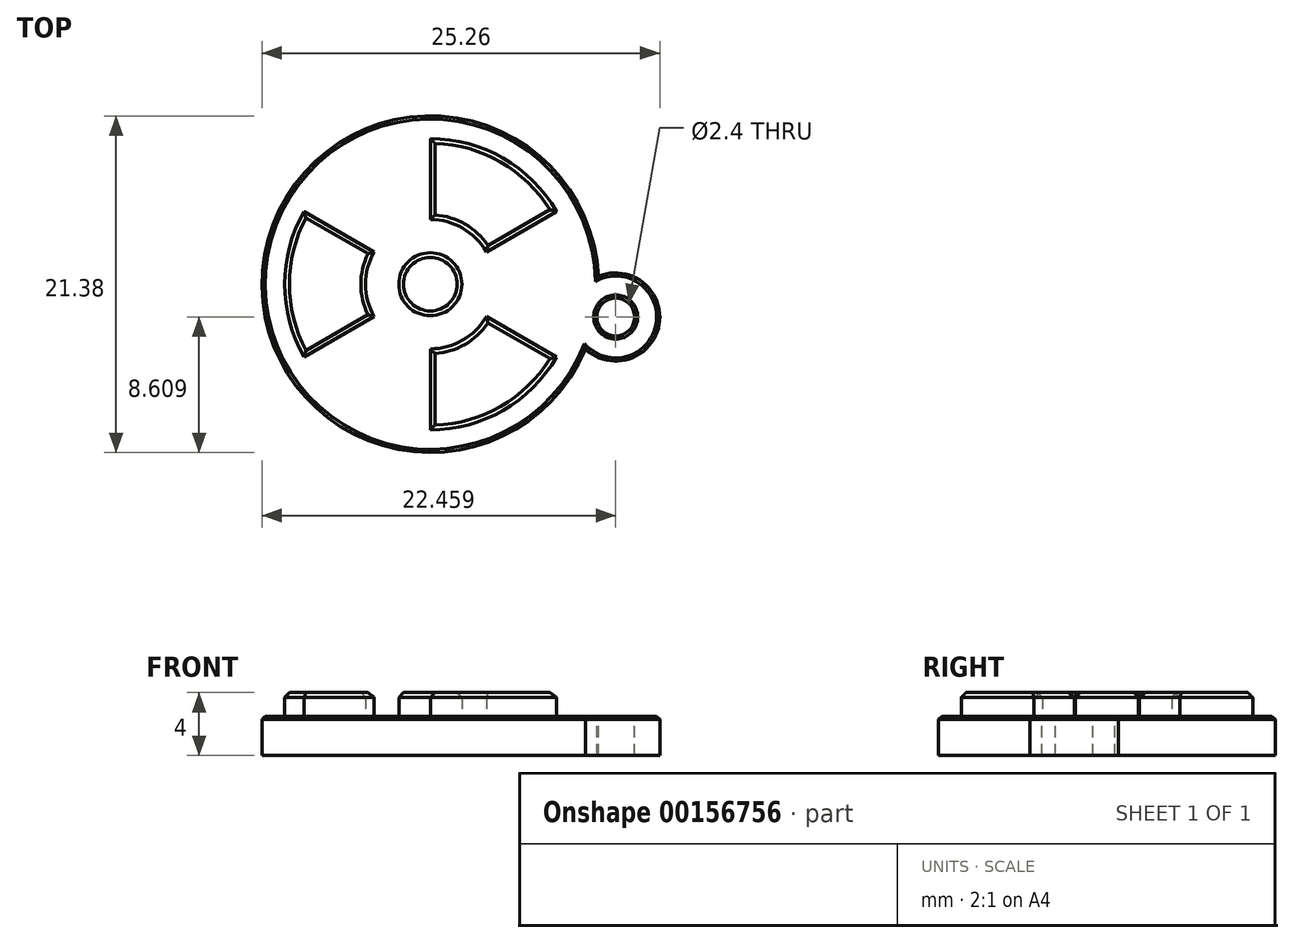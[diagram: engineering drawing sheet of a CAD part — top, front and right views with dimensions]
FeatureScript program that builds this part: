
annotation { "Feature Type Name" : "Feature", "Feature Type Description" : "" }
export const myFeature = defineFeature(function(context is Context, id is Id, definition is map)
    precondition{}
    {
        {
            var Q0;
            Q0=qCreatedBy(makeId("Top.planeOp"),FACE);
            var sketch = newSketch(context, id + "F0", { "sketchPlane" : qUnion([Q0])});
            skCircle(sketch, "E0", {"center": v(45.51, 145.43) * mm, "radius": 2 * mm});
            skCircle(sketch, "E1.cCircle", {"center": v(45.51, 145.43) * mm, "radius": 4.11 * mm});
            skLineSegment(sketch, "E1.0", {"start": v(49.63, 147.8) * mm, "end": v(49.63, 143.06) * mm, "construction": true});
            skLineSegment(sketch, "E1.1", {"start": v(49.63, 143.06) * mm, "end": v(45.51, 140.68) * mm, "construction": true});
            skLineSegment(sketch, "E1.2", {"start": v(45.51, 140.68) * mm, "end": v(41.4, 143.06) * mm, "construction": true});
            skLineSegment(sketch, "E1.3", {"start": v(41.4, 143.06) * mm, "end": v(41.4, 147.8) * mm, "construction": true});
            skLineSegment(sketch, "E1.4", {"start": v(41.4, 147.8) * mm, "end": v(45.51, 150.18) * mm, "construction": true});
            skLineSegment(sketch, "E1.5", {"start": v(45.51, 150.18) * mm, "end": v(49.63, 147.8) * mm, "construction": true});
            skPoint(sketch, "E1.0.midPoint", {"position": v(49.63, 145.43) * mm});
            skCircle(sketch, "E2.cCircle", {"center": v(45.51, 145.43) * mm, "radius": 9.25 * mm});
            skLineSegment(sketch, "E2.0", {"start": v(54.77, 150.77) * mm, "end": v(54.77, 140.09) * mm, "construction": true});
            skLineSegment(sketch, "E2.1", {"start": v(54.77, 140.09) * mm, "end": v(45.51, 134.75) * mm, "construction": true});
            skLineSegment(sketch, "E2.2", {"start": v(45.51, 134.75) * mm, "end": v(36.26, 140.09) * mm, "construction": true});
            skLineSegment(sketch, "E2.3", {"start": v(36.26, 140.09) * mm, "end": v(36.26, 150.77) * mm, "construction": true});
            skLineSegment(sketch, "E2.4", {"start": v(36.26, 150.77) * mm, "end": v(45.51, 156.11) * mm, "construction": true});
            skLineSegment(sketch, "E2.5", {"start": v(45.51, 156.11) * mm, "end": v(54.77, 150.77) * mm, "construction": true});
            skPoint(sketch, "E2.0.midPoint", {"position": v(54.77, 145.43) * mm});
            skLineSegment(sketch, "E3", {"start": v(41.4, 147.8) * mm, "end": v(36.26, 150.77) * mm});
            skLineSegment(sketch, "E4", {"start": v(41.4, 143.06) * mm, "end": v(36.26, 140.09) * mm});
            skLineSegment(sketch, "E5", {"start": v(45.51, 140.68) * mm, "end": v(45.51, 134.75) * mm});
            skLineSegment(sketch, "E6", {"start": v(49.63, 143.06) * mm, "end": v(54.77, 140.09) * mm});
            skLineSegment(sketch, "E7", {"start": v(49.63, 147.8) * mm, "end": v(54.77, 150.77) * mm});
            skLineSegment(sketch, "E8", {"start": v(45.51, 150.18) * mm, "end": v(45.51, 156.11) * mm});
            skLineSegment(sketch, "E9", {"start": v(41.4, 143.06) * mm, "end": v(41.95, 143.38) * mm});
            skLineSegment(sketch, "E10", {"start": v(41.4, 147.8) * mm, "end": v(41.95, 147.49) * mm});
            skLineSegment(sketch, "E11", {"start": v(45.51, 140.68) * mm, "end": v(45.51, 141.32) * mm});
            skLineSegment(sketch, "E12", {"start": v(49.63, 143.06) * mm, "end": v(49.07, 143.38) * mm});
            skLineSegment(sketch, "E13", {"start": v(49.63, 147.8) * mm, "end": v(49.07, 147.49) * mm});
            skLineSegment(sketch, "E14", {"start": v(45.51, 150.18) * mm, "end": v(45.51, 149.54) * mm});
            skSolve(sketch);
        }
        {
            var Q0;
            {var subQ6=sQuery(id+"F0.wireOp",EDGE,"E13");Q0=makeQuery(id+"F0.imprint","IMPRINT",FACE,{"disambiguationData":[TD([[makeQuery(id+"F0.imprint","IMPRINT",EDGE,{"derivedFrom":subQ6}),-1.0]])]});}
            var Q1;
            {var subQ0=sQuery(id+"F0.wireOp",EDGE,"E9");Q1=makeQuery(id+"F0.imprint","IMPRINT",FACE,{"disambiguationData":[TD([[makeQuery(id+"F0.imprint","IMPRINT",EDGE,{"derivedFrom":subQ0}),1.0]])]});}
            var Q2;
            {var subQ4=sQuery(id+"F0.wireOp",EDGE,"E11");Q2=makeQuery(id+"F0.imprint","IMPRINT",FACE,{"disambiguationData":[TD([[makeQuery(id+"F0.imprint","IMPRINT",EDGE,{"derivedFrom":subQ4}),-1.0]])]});}
            var Q3;
            Q3=makeQuery(id+"F0.imprint","IMPRINT",FACE,{"disambiguationData":[TD([[makeQuery(id+"F0.imprint","IMPRINT",EDGE,{"derivedFrom":sQuery(id+"F0.wireOp",EDGE,"E0")}),1.0]])]});
            extrude(context, id + "F1", {"entities" : qUnion([Q0, Q1, Q2, Q3]), "depth" : 1.5 * mm});
        }
        {
            var Q0;
            Q0=qCreatedBy(makeId("Top.planeOp"),FACE);
            var sketch = newSketch(context, id + "F2", { "sketchPlane" : qUnion([Q0])});
            skCircle(sketch, "E15.0.0", {"center": v(45.51, 145.43) * mm, "radius": 2 * mm});
            skCircle(sketch, "E16", {"center": v(45.51, 145.43) * mm, "radius": 10.69 * mm});
            skArc(sketch, "E17", {"start": v(55.37, 141.3) * mm, "mid": v(60.05, 142.86) * mm, "end": v(56.2, 145.93) * mm});
            skCircle(sketch, "E18", {"center": v(57.29, 143.35) * mm, "radius": 1.2 * mm});
            skSolve(sketch);
        }
        {
            var Q0;
            Q0 = qSketchRegion(id + "F2", true);
            var Q1;
            Q1=makeQuery(id+"F2.imprint","IMPRINT",FACE,{"disambiguationData":[TD([[makeQuery(id+"F2.imprint","IMPRINT",EDGE,{"derivedFrom":sQuery(id+"F2.wireOp",EDGE,"E15.0.0")}),1.0]])]});
            extrude(context, id + "F3", {"entities" : qUnion([Q0, Q1]), "oppositeDirection" : true, "depth" : 2.5 * mm});
        }
        {
            var Q0;
            Q0=makeQuery(id+"F1.opExtrude","CAP_FACE",FACE,{"disambiguationData":[OSD([sQuery(id+"F0.wireOp",EDGE,"E1.cCircle"),sQuery(id+"F0.wireOp",EDGE,"E2.cCircle"),sQuery(id+"F0.wireOp",EDGE,"E3"),sQuery(id+"F0.wireOp",EDGE,"E4"),sQuery(id+"F0.wireOp",EDGE,"E9"),sQuery(id+"F0.wireOp",EDGE,"E10")])],"isStart":false});
            var Q1;
            Q1=makeQuery(id+"F1.opExtrude","CAP_FACE",FACE,{"disambiguationData":[OSD([sQuery(id+"F0.wireOp",EDGE,"E1.cCircle"),sQuery(id+"F0.wireOp",EDGE,"E2.cCircle"),sQuery(id+"F0.wireOp",EDGE,"E5"),sQuery(id+"F0.wireOp",EDGE,"E6"),sQuery(id+"F0.wireOp",EDGE,"E11"),sQuery(id+"F0.wireOp",EDGE,"E12")])],"isStart":false});
            var Q2;
            Q2=makeQuery(id+"F1.opExtrude","CAP_FACE",FACE,{"disambiguationData":[OSD([sQuery(id+"F0.wireOp",EDGE,"E1.cCircle"),sQuery(id+"F0.wireOp",EDGE,"E2.cCircle"),sQuery(id+"F0.wireOp",EDGE,"E7"),sQuery(id+"F0.wireOp",EDGE,"E8"),sQuery(id+"F0.wireOp",EDGE,"E13"),sQuery(id+"F0.wireOp",EDGE,"E14")])],"isStart":false});
            var Q3;
            Q3=makeQuery(id+"F1.opExtrude","CAP_FACE",FACE,{"disambiguationData":[OSD([sQuery(id+"F0.wireOp",EDGE,"E0")])],"isStart":false});
            chamfer(context, id + "F4", {"entities" : qUnion([Q0, Q1, Q2, Q3]), "width" : 0.3 * mm, "tangentPropagation" : true});
        }
        {
            var Q0;
            Q0=makeQuery(id+"F3.opExtrude","CAP_FACE",FACE,{"disambiguationData":[OSD([sQuery(id+"F2.wireOp",EDGE,"E16"),sQuery(id+"F2.wireOp",EDGE,"E17"),sQuery(id+"F2.wireOp",EDGE,"E18")])],"isStart":true});
            chamfer(context, id + "F5", {"entities" : qUnion([Q0]), "width" : 0.2 * mm, "tangentPropagation" : true});
        }
    });
